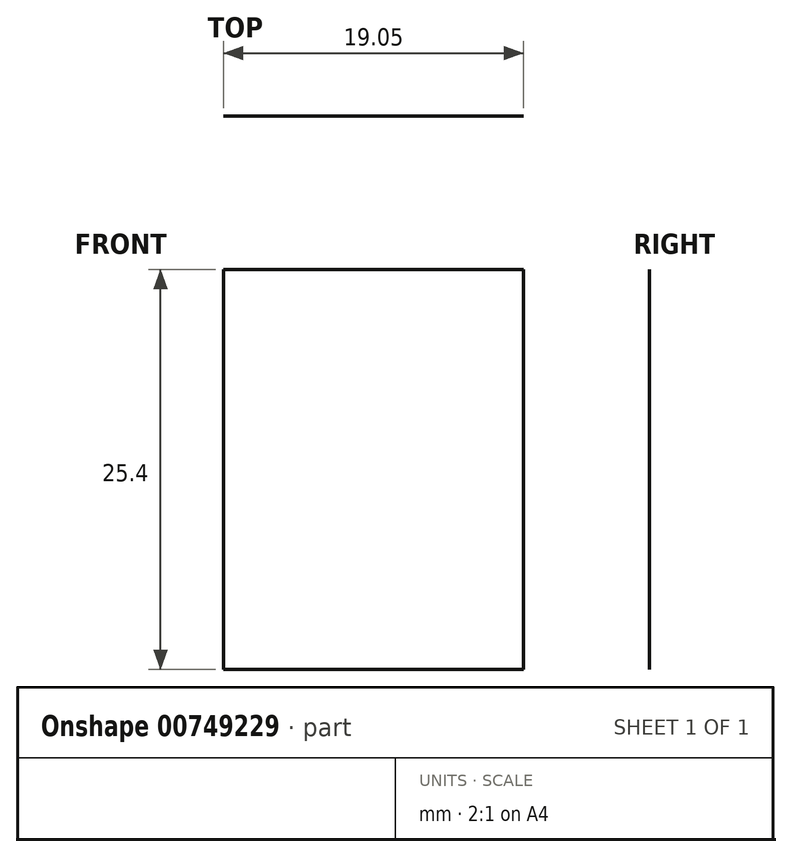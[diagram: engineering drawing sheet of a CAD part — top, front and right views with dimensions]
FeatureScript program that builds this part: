
annotation { "Feature Type Name" : "Feature", "Feature Type Description" : "" }
export const myFeature = defineFeature(function(context is Context, id is Id, definition is map)
    precondition{}
    {
        {
            var Q0;
            Q0=qCreatedBy(makeId("Top.planeOp"),FACE);
            var sketch = newSketch(context, id + "F0", { "sketchPlane" : qUnion([Q0])});
            skCircle(sketch, "E0", {"center": v(0, 0) * mm, "radius": 12.7 * mm});
            skLineSegment(sketch, "E1", {"start": v(0, 0) * mm, "end": v(25.4, 0) * mm});
            skLineSegment(sketch, "E2", {"start": v(25.4, 0) * mm, "end": v(25.4, -25.4) * mm});
            skLineSegment(sketch, "E3", {"start": v(25.4, 0) * mm, "end": v(25.4, 12.7) * mm});
            skLineSegment(sketch, "E4", {"start": v(25.4, -25.4) * mm, "end": v(-50.8, -25.4) * mm});
            skLineSegment(sketch, "E5", {"start": v(-50.8, -25.4) * mm, "end": v(-50.8, -19.05) * mm});
            skLineSegment(sketch, "E6", {"start": v(-50.8, -19.05) * mm, "end": v(-31.75, -19.05) * mm});
            skLineSegment(sketch, "E7", {"start": v(-31.75, -19.05) * mm, "end": v(-31.75, -6.35) * mm});
            skLineSegment(sketch, "E8", {"start": v(-31.75, -6.35) * mm, "end": v(-50.8, -6.35) * mm});
            skLineSegment(sketch, "E9", {"start": v(-50.8, -6.35) * mm, "end": v(-50.8, 19.05) * mm});
            skLineSegment(sketch, "E10", {"start": v(25.4, 12.7) * mm, "end": v(25.4, 25.4) * mm});
            skLineSegment(sketch, "E11", {"start": v(25.4, 25.4) * mm, "end": v(6.35, 25.4) * mm});
            skLineSegment(sketch, "E12", {"start": v(6.35, 25.4) * mm, "end": v(-19.05, 25.4) * mm});
            skLineSegment(sketch, "E13", {"start": v(6.35, 25.4) * mm, "end": v(25.4, 12.7) * mm});
            skLineSegment(sketch, "E14", {"start": v(-50.8, 19.05) * mm, "end": v(-19.05, 25.4) * mm});
            skSolve(sketch);
        }
        {
            var Q0;
            Q0=sQuery(id+"F0.wireOp",EDGE,"E11");
            extrude(context, id + "F1", {"bodyType" : ToolBodyType.SURFACE, "surfaceEntities" : qUnion([Q0]), "depth" : 25.4 * mm, "offsetDistance" : 25.4 * mm});
        }
    });
